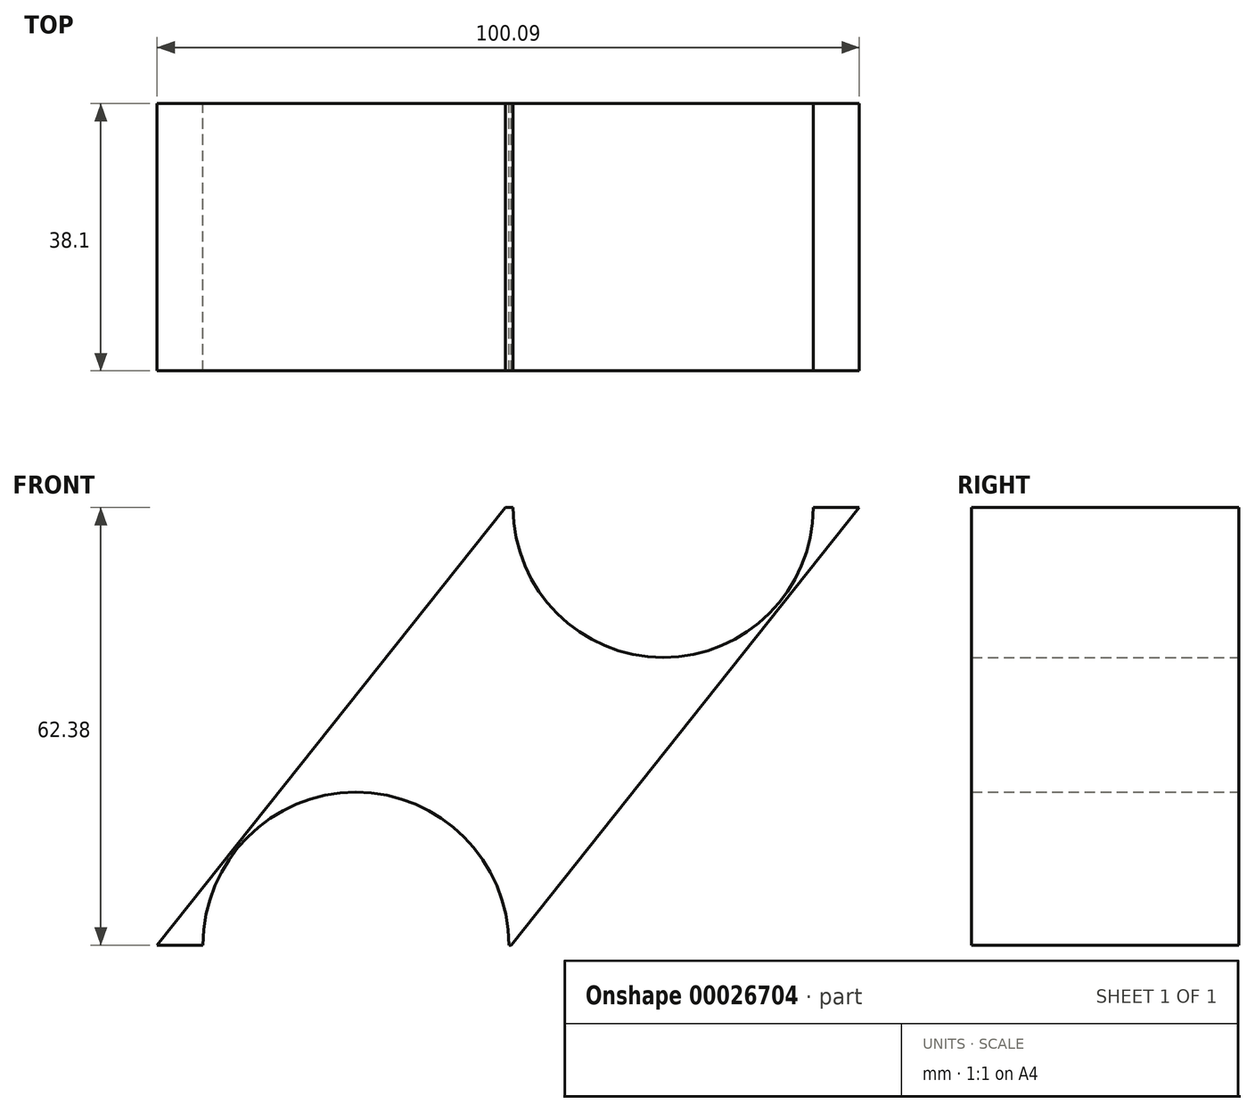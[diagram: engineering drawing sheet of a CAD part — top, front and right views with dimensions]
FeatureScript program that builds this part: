
annotation { "Feature Type Name" : "Feature", "Feature Type Description" : "" }
export const myFeature = defineFeature(function(context is Context, id is Id, definition is map)
    precondition{}
    {
        {
            var Q0;
            Q0=qCreatedBy(makeId("Front.planeOp"),FACE);
            var sketch = newSketch(context, id + "F0", { "sketchPlane" : qUnion([Q0])});
            skLineSegment(sketch, "E0", {"start": v(-22.52, 54.44) * mm, "end": v(-72.14, -7.94) * mm});
            skLineSegment(sketch, "E1", {"start": v(-72.14, -7.94) * mm, "end": v(-65.6, -7.94) * mm});
            skLineSegment(sketch, "E2", {"start": v(-21.67, -7.94) * mm, "end": v(27.95, 54.44) * mm});
            skLineSegment(sketch, "E3", {"start": v(27.95, 54.44) * mm, "end": v(21.38, 54.44) * mm});
            skArc(sketch, "E4", {"start": v(-21.38, 54.44) * mm, "mid": v(0, 33.06) * mm, "end": v(21.38, 54.44) * mm});
            skLineSegment(sketch, "E5.trimOffspring", {"start": v(-21.38, 54.44) * mm, "end": v(-22.52, 54.44) * mm});
            skArc(sketch, "E6", {"start": v(-22, -7.94) * mm, "mid": v(-43.8, 13.85) * mm, "end": v(-65.6, -7.94) * mm});
            skLineSegment(sketch, "E7.trimOffspring", {"start": v(-22, -7.94) * mm, "end": v(-21.67, -7.94) * mm});
            skSolve(sketch);
        }
        {
            var Q0;
            Q0 = qSketchRegion(id + "F0", true);
            extrude(context, id + "F1", {"entities" : qUnion([Q0]), "depth" : 38.1 * mm});
        }
    });
